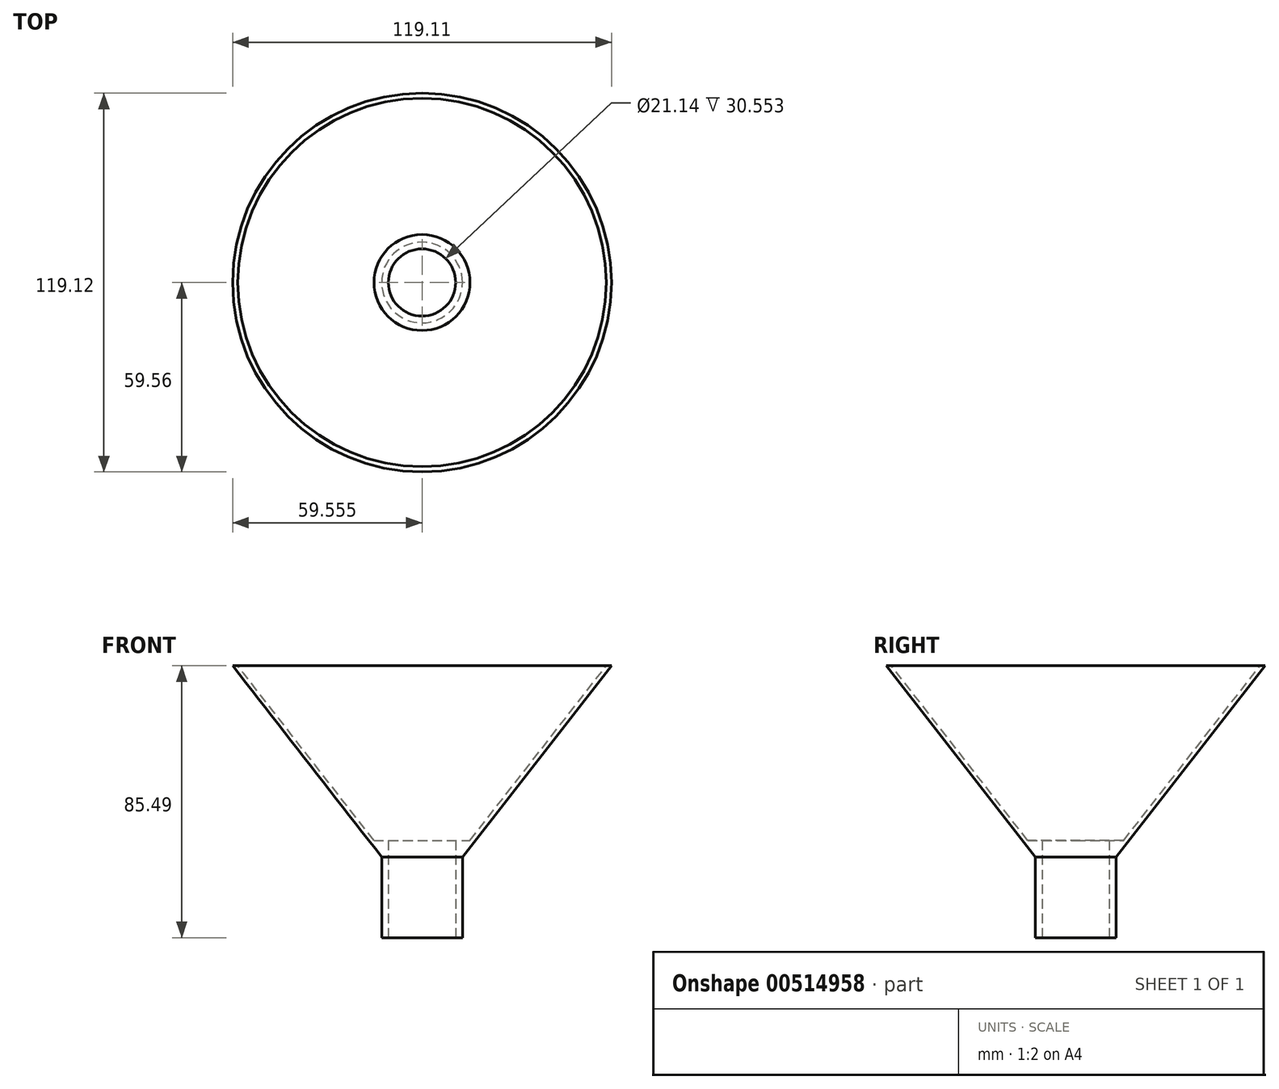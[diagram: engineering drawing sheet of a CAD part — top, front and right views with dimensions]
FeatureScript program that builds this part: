
annotation { "Feature Type Name" : "Feature", "Feature Type Description" : "" }
export const myFeature = defineFeature(function(context is Context, id is Id, definition is map)
    precondition{}
    {
        {
            var Q0;
            Q0=qCreatedBy(makeId("Front.planeOp"),FACE);
            var sketch = newSketch(context, id + "F0", { "sketchPlane" : qUnion([Q0])});
            skLineSegment(sketch, "E0", {"start": v(21.67, -30.55) * mm, "end": v(21.67, -5.15) * mm});
            skLineSegment(sketch, "E1", {"start": v(21.67, -5.15) * mm, "end": v(68.53, 54.94) * mm});
            skLineSegment(sketch, "E2", {"start": v(21.67, -30.55) * mm, "end": v(8.97, -30.55) * mm});
            skLineSegment(sketch, "E3", {"start": v(8.97, -30.55) * mm, "end": v(8.97, 0) * mm});
            skLineSegment(sketch, "E4", {"start": v(8.97, 0) * mm, "end": v(24.07, 0) * mm});
            skLineSegment(sketch, "E5", {"start": v(24.07, 0) * mm, "end": v(66.91, 54.94) * mm});
            skLineSegment(sketch, "E6", {"start": v(66.91, 54.94) * mm, "end": v(68.53, 54.94) * mm});
            skSolve(sketch);
        }
        {
            var Q0;
            Q0 = qSketchRegion(id + "F0", true);
            var Q1;
            Q1=sQuery(id+"F0.wireOp",EDGE,"E3");
            revolve(context, id + "F1", {"entities" : qUnion([Q0]), "axis" : qUnion([Q1]), "revolveType" : RevolveType.FULL});
        }
        {
            var Q0;
            Q0=makeQuery(id+"F1.opRevolve","SWEPT_FACE",FACE,{"disambiguationData":[OSD([sQuery(id+"F0.wireOp",EDGE,"E2")])]});
            var sketch = newSketch(context, id + "F2", { "sketchPlane" : qUnion([Q0])});
            skCircle(sketch, "E7", {"center": v(8.97, 0) * mm, "radius": 10.57 * mm});
            skSolve(sketch);
        }
        {
            var Q0;
            Q0 = qSketchRegion(id + "F2", true);
            extrude(context, id + "F3", {"entities" : qUnion([Q0]), "operationType" : NewBodyOperationType.REMOVE, "oppositeDirection" : true, "depth" : 22.86 * mm, "offsetDistance" : 25.4 * mm});
        }
        {
            var Q0;
            Q0=makeQuery(id+"F3.boolean.opBoolean","COPY",FACE,{"derivedFrom":makeQuery(id+"F3.opExtrude","CAP_FACE",FACE,{"disambiguationData":[OSD([sQuery(id+"F2.wireOp",EDGE,"E7")])],"isStart":false})});
            var sketch = newSketch(context, id + "F4", { "sketchPlane" : qUnion([Q0])});
            skSolve(sketch);
        }
        {
            var Q0;
            Q0 = qSketchRegion(id + "F4", true);
            var Q1;
            Q1=makeQuery(id+"F4.imprint","IMPRINT",FACE,{"disambiguationData":[TD([[makeQuery(id+"F4.imprint","IMPRINT",EDGE,{"derivedFrom":makeQuery(id+"F3.boolean.opBoolean","COPY",EDGE,{"derivedFrom":makeQuery(id+"F3.opExtrude","CAP_EDGE",EDGE,{"disambiguationData":[OSD([sQuery(id+"F2.wireOp",EDGE,"E7")])],"isStart":false})})}),1.0]])]});
            extrude(context, id + "F5", {"entities" : qUnion([Q0, Q1]), "operationType" : NewBodyOperationType.REMOVE, "oppositeDirection" : true, "depth" : 25.4 * mm, "offsetDistance" : 25.4 * mm});
        }
    });
